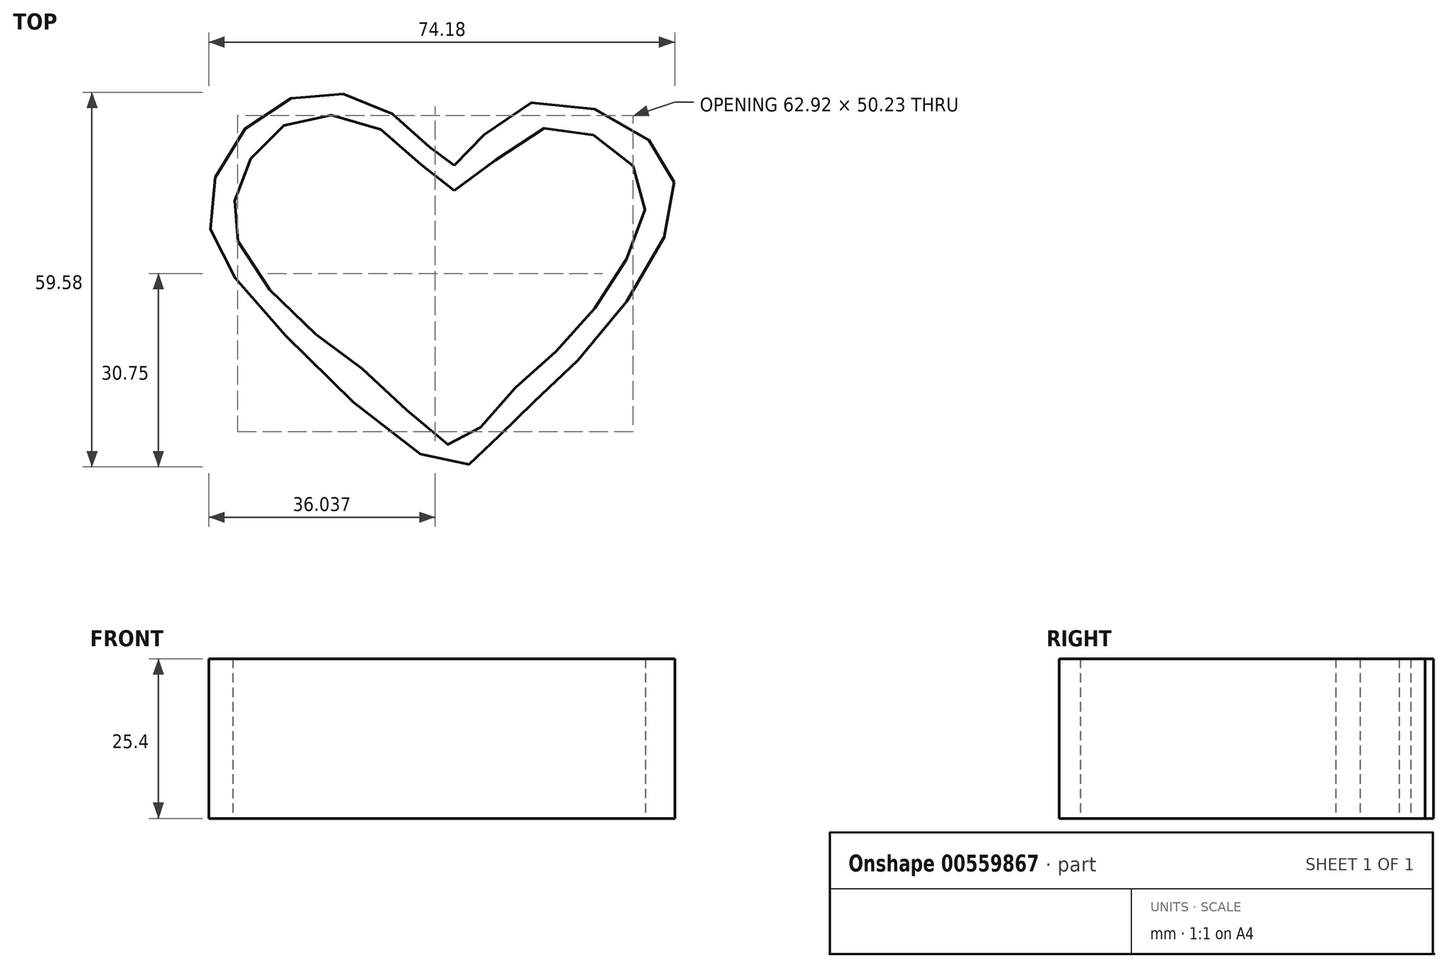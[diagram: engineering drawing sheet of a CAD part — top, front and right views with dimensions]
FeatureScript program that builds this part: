
annotation { "Feature Type Name" : "Feature", "Feature Type Description" : "" }
export const myFeature = defineFeature(function(context is Context, id is Id, definition is map)
    precondition{}
    {
        {
            var Q0;
            Q0=qCreatedBy(makeId("Top.planeOp"),FACE);
            var sketch = newSketch(context, id + "F0", { "sketchPlane" : qUnion([Q0])});
            skFitSpline(sketch, "E0", {"points": [v(0, 0) * mm, v(-7.33, 6.41) * mm, v(-18.93, 11.9) * mm, v(-29.32, 8.86) * mm, v(-34.5, 0) * mm, v(-34.5, -7.94) * mm, v(-23.51, -21.68) * mm, v(-10.69, -31.76) * mm, v(0, -40.62) * mm, v(6.72, -34.5) * mm, v(17.1, -24.74) * mm, v(26.87, -11.9) * mm, v(30.23, 0) * mm, v(23.2, 8.25) * mm, v(11.6, 8.86) * mm, v(0, 0) * mm]});
            skFitSpline(sketch, "E1", {"points": [v(0, 3.97) * mm, v(-4.58, 7.63) * mm, v(-17.1, 15.27) * mm, v(-31.76, 11.3) * mm, v(-39.09, -3.66) * mm, v(-29.01, -20.77) * mm, v(0, -43.97) * mm, v(7.33, -38.78) * mm, v(19.24, -27.48) * mm, v(34.81, -3.05) * mm, v(29.93, 8.86) * mm, v(9.77, 13.13) * mm, v(0, 3.97) * mm]});
            skSolve(sketch);
        }
        {
            var Q0;
            Q0 = qSketchRegion(id + "F0", true);
            extrude(context, id + "F1", {"entities" : qUnion([Q0]), "depth" : 25.4 * mm, "offsetDistance" : 25.4 * mm});
        }
    });
